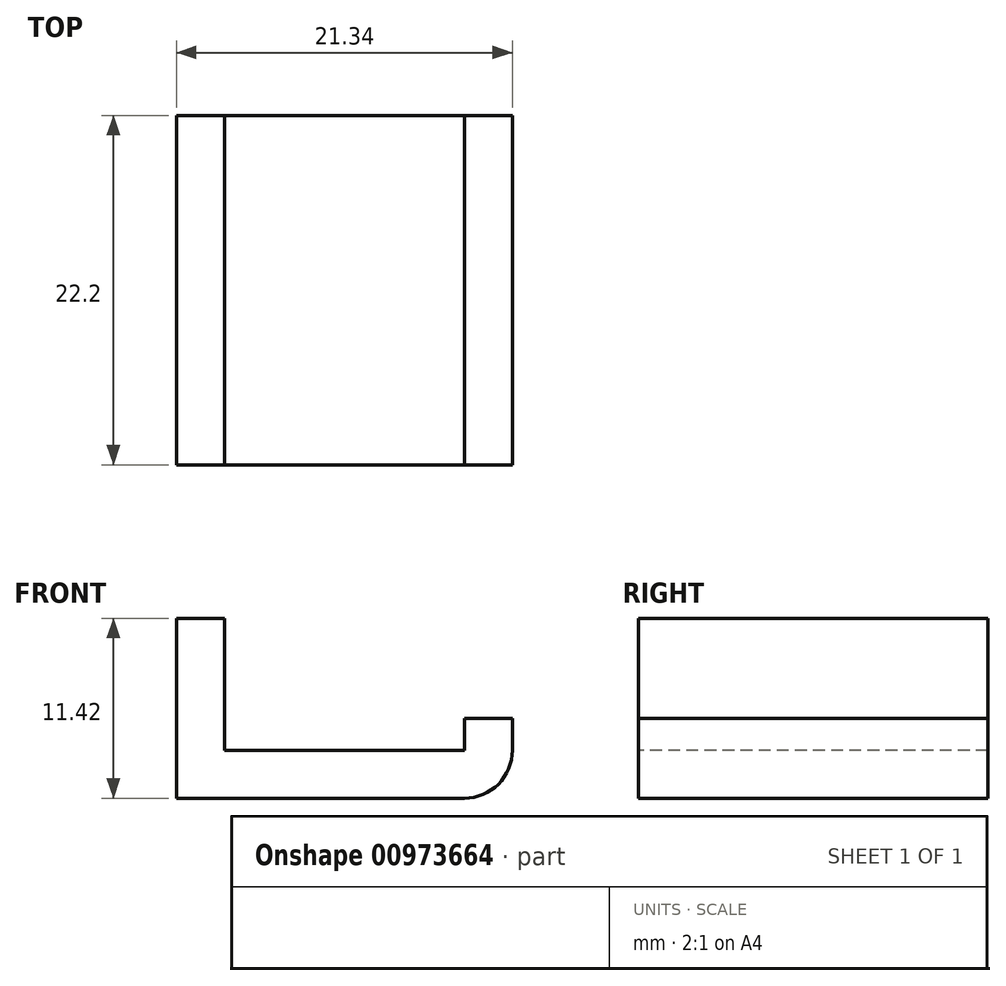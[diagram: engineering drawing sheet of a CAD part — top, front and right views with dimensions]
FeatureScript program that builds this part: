
annotation { "Feature Type Name" : "Feature", "Feature Type Description" : "" }
export const myFeature = defineFeature(function(context is Context, id is Id, definition is map)
    precondition{}
    {
        {
            var Q0;
            Q0=qCreatedBy(makeId("Front.planeOp"),FACE);
            var sketch = newSketch(context, id + "F0", { "sketchPlane" : qUnion([Q0])});
            skLineSegment(sketch, "E0.bottom", {"start": v(-10.67, 5.72) * mm, "end": v(10.67, 5.72) * mm});
            skLineSegment(sketch, "E0.top", {"start": v(-10.67, -5.72) * mm, "end": v(10.67, -5.72) * mm});
            skLineSegment(sketch, "E0.left", {"start": v(-10.67, 5.72) * mm, "end": v(-10.67, -5.71) * mm});
            skLineSegment(sketch, "E0.right", {"start": v(10.67, 5.72) * mm, "end": v(10.67, -5.71) * mm});
            skPoint(sketch, "E0.middle", {"position": v(0, 0) * mm});
            skSolve(sketch);
        }
        {
            var Q0;
            Q0=makeQuery(id+"F0.imprint","IMPRINT",FACE,{"disambiguationData":[TD([[makeQuery(id+"F0.imprint","IMPRINT",EDGE,{"derivedFrom":sQuery(id+"F0.wireOp",EDGE,"E0.bottom")}),-1.0]])]});
            extrude(context, id + "F1", {"entities" : qUnion([Q0]), "oppositeDirection" : true, "depth" : 22.2 * mm, "offsetDistance" : 25.4 * mm});
        }
        {
            var Q0;
            Q0=makeQuery(id+"F1.opExtrude","CAP_FACE",FACE,{"disambiguationData":[OSD([sQuery(id+"F0.wireOp",EDGE,"E0.bottom"),sQuery(id+"F0.wireOp",EDGE,"E0.top"),sQuery(id+"F0.wireOp",EDGE,"E0.left"),sQuery(id+"F0.wireOp",EDGE,"E0.right")])],"isStart":true});
            var sketch = newSketch(context, id + "F2", { "sketchPlane" : qUnion([Q0])});
            skLineSegment(sketch, "E1.bottom", {"start": v(-7.62, 5.72) * mm, "end": v(7.62, 5.72) * mm});
            skLineSegment(sketch, "E1.top", {"start": v(-7.62, -2.67) * mm, "end": v(7.62, -2.67) * mm});
            skLineSegment(sketch, "E1.left", {"start": v(-7.62, 5.72) * mm, "end": v(-7.62, -2.67) * mm});
            skLineSegment(sketch, "E1.right", {"start": v(7.62, 5.72) * mm, "end": v(7.62, -2.67) * mm});
            skSolve(sketch);
        }
        {
            var Q0;
            Q0=makeQuery(id+"F2.imprint","IMPRINT",FACE,{"disambiguationData":[TD([[makeQuery(id+"F2.imprint","IMPRINT",EDGE,{"derivedFrom":sQuery(id+"F2.wireOp",EDGE,"E1.bottom")}),-1.0]])]});
            extrude(context, id + "F3", {"entities" : qUnion([Q0]), "operationType" : NewBodyOperationType.REMOVE, "oppositeDirection" : true, "depth" : 25.4 * mm, "offsetDistance" : 25.4 * mm});
        }
        {
            var Q0;
            Q0=makeQuery(id+"F1.opExtrude","CAP_FACE",FACE,{"disambiguationData":[OSD([sQuery(id+"F0.wireOp",EDGE,"E0.bottom"),sQuery(id+"F0.wireOp",EDGE,"E0.top"),sQuery(id+"F0.wireOp",EDGE,"E0.left"),sQuery(id+"F0.wireOp",EDGE,"E0.right")])],"isStart":true});
            var sketch = newSketch(context, id + "F4", { "sketchPlane" : qUnion([Q0])});
            skLineSegment(sketch, "E2.bottom", {"start": v(10.67, -5.71) * mm, "end": v(7.62, -5.71) * mm});
            skLineSegment(sketch, "E2.top", {"start": v(10.67, -0.63) * mm, "end": v(7.62, -0.63) * mm});
            skLineSegment(sketch, "E2.left", {"start": v(10.67, -5.71) * mm, "end": v(10.67, -0.63) * mm});
            skLineSegment(sketch, "E2.right", {"start": v(7.62, -5.71) * mm, "end": v(7.62, -0.63) * mm});
            skSolve(sketch);
        }
        {
            var Q0;
            {var subQ0=sQuery(id+"F4.wireOp",EDGE,"E2.top");Q0=makeQuery(id+"F4.imprint","IMPRINT",FACE,{"disambiguationData":[TD([[makeQuery(id+"F4.imprint","IMPRINT",EDGE,{"derivedFrom":subQ0}),-1.0]])]});}
            extrude(context, id + "F5", {"entities" : qUnion([Q0]), "operationType" : NewBodyOperationType.REMOVE, "oppositeDirection" : true, "depth" : 25.4 * mm, "offsetDistance" : 25.4 * mm});
        }
        {
            var Q0;
            Q0=makeQuery(id+"F1.opExtrude","SWEPT_EDGE",EDGE,{"disambiguationData":[OSD([sQuery(id+"F0.wireOp",EDGE,"E0.top"),sQuery(id+"F0.wireOp",EDGE,"E0.right")])]});
            fillet(context, id + "F6", {"entities" : qUnion([Q0]), "radius" : 3.05 * mm, "tangentPropagation" : true, "allowEdgeOverflow" : false});
        }
    });
